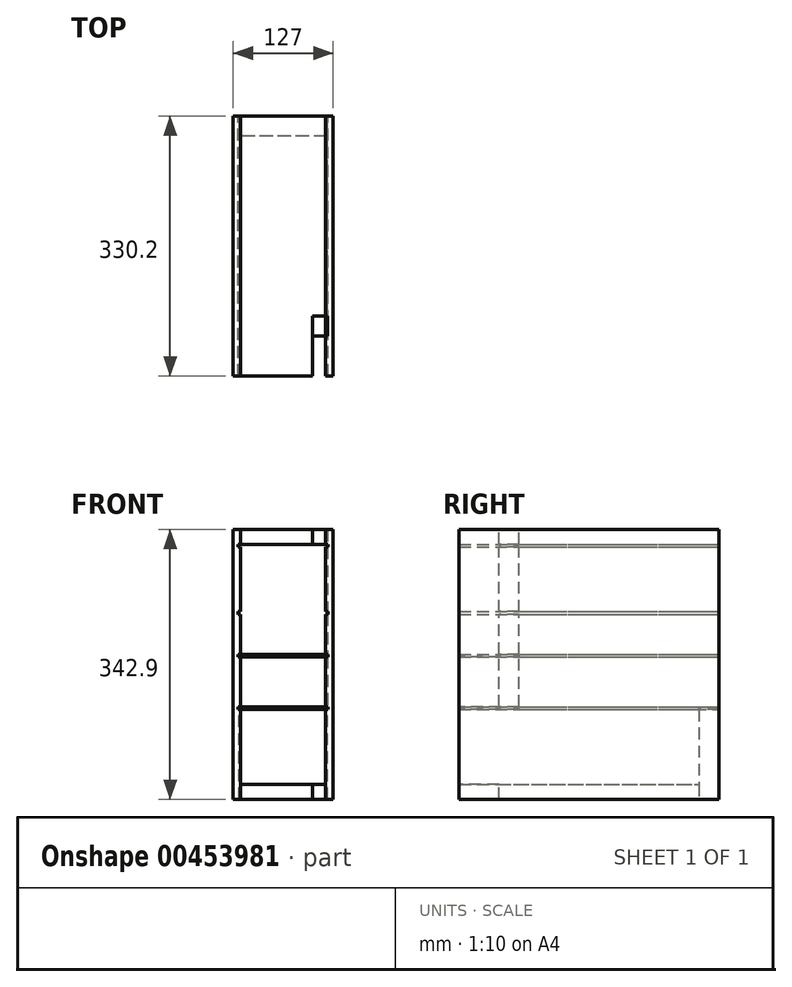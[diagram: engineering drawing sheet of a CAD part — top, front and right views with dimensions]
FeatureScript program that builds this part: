
annotation { "Feature Type Name" : "Feature", "Feature Type Description" : "" }
export const myFeature = defineFeature(function(context is Context, id is Id, definition is map)
    precondition{}
    {
        {
            var Q0;
            Q0=qCreatedBy(makeId("Front.planeOp"),FACE);
            var sketch = newSketch(context, id + "F0", { "sketchPlane" : qUnion([Q0])});
            skLineSegment(sketch, "E0.bottom", {"start": v(0, 0) * mm, "end": v(9.52, 0) * mm});
            skLineSegment(sketch, "E0.top", {"start": v(0, 342.9) * mm, "end": v(9.52, 342.9) * mm});
            skLineSegment(sketch, "E0.left", {"start": v(0, 0) * mm, "end": v(0, 342.9) * mm});
            skLineSegment(sketch, "E0.right", {"start": v(9.52, 0) * mm, "end": v(9.52, 342.9) * mm});
            skLineSegment(sketch, "E1.bottom", {"start": v(9.52, 0) * mm, "end": v(117.48, 0) * mm});
            skLineSegment(sketch, "E1.top", {"start": v(9.52, 19.05) * mm, "end": v(117.48, 19.05) * mm});
            skLineSegment(sketch, "E1.left", {"start": v(9.52, 0) * mm, "end": v(9.52, 19.05) * mm});
            skLineSegment(sketch, "E1.right", {"start": v(117.48, 0) * mm, "end": v(117.48, 19.05) * mm});
            skLineSegment(sketch, "E2.bottom", {"start": v(117.48, 0) * mm, "end": v(127, 0) * mm});
            skLineSegment(sketch, "E2.top", {"start": v(117.47, 342.9) * mm, "end": v(127, 342.9) * mm});
            skLineSegment(sketch, "E2.left", {"start": v(117.48, 0) * mm, "end": v(117.47, 342.9) * mm});
            skLineSegment(sketch, "E2.right", {"start": v(127, 0) * mm, "end": v(127, 342.9) * mm});
            skLineSegment(sketch, "E3.bottom", {"start": v(9.52, 342.9) * mm, "end": v(117.47, 342.9) * mm});
            skLineSegment(sketch, "E3.top", {"start": v(9.52, 323.85) * mm, "end": v(117.47, 323.85) * mm});
            skLineSegment(sketch, "E3.left", {"start": v(9.52, 342.9) * mm, "end": v(9.52, 323.85) * mm});
            skLineSegment(sketch, "E3.right", {"start": v(117.47, 342.9) * mm, "end": v(117.47, 323.85) * mm});
            skLineSegment(sketch, "E4.bottom", {"start": v(117.47, 117.6) * mm, "end": v(120.65, 117.6) * mm});
            skLineSegment(sketch, "E4.top", {"start": v(117.47, 114.3) * mm, "end": v(120.65, 114.3) * mm});
            skLineSegment(sketch, "E4.left", {"start": v(117.47, 117.6) * mm, "end": v(117.47, 114.3) * mm});
            skLineSegment(sketch, "E4.right", {"start": v(120.65, 117.6) * mm, "end": v(120.65, 114.3) * mm});
            skLineSegment(sketch, "E5.bottom", {"start": v(9.52, 114.3) * mm, "end": v(6.35, 114.3) * mm});
            skLineSegment(sketch, "E5.top", {"start": v(9.52, 117.6) * mm, "end": v(6.35, 117.6) * mm});
            skLineSegment(sketch, "E5.left", {"start": v(9.52, 114.3) * mm, "end": v(9.52, 117.6) * mm});
            skLineSegment(sketch, "E5.right", {"start": v(6.35, 114.3) * mm, "end": v(6.35, 117.6) * mm});
            skLineSegment(sketch, "E6", {"start": v(9.52, 114.3) * mm, "end": v(117.47, 114.3) * mm, "construction": true});
            skLineSegment(sketch, "E7", {"start": v(117.47, 117.6) * mm, "end": v(9.52, 117.6) * mm, "construction": true});
            skLineSegment(sketch, "E8.bottom", {"start": v(9.52, 184.4) * mm, "end": v(6.35, 184.4) * mm});
            skLineSegment(sketch, "E8.top", {"start": v(9.52, 181.1) * mm, "end": v(6.35, 181.1) * mm});
            skLineSegment(sketch, "E8.left", {"start": v(9.52, 184.4) * mm, "end": v(9.52, 181.1) * mm});
            skLineSegment(sketch, "E8.right", {"start": v(6.35, 184.4) * mm, "end": v(6.35, 181.1) * mm});
            skLineSegment(sketch, "E9.bottom", {"start": v(117.47, 184.4) * mm, "end": v(120.65, 184.4) * mm});
            skLineSegment(sketch, "E9.top", {"start": v(117.47, 181.1) * mm, "end": v(120.65, 181.1) * mm});
            skLineSegment(sketch, "E9.left", {"start": v(117.47, 184.4) * mm, "end": v(117.47, 181.1) * mm});
            skLineSegment(sketch, "E9.right", {"start": v(120.65, 184.4) * mm, "end": v(120.65, 181.1) * mm});
            skLineSegment(sketch, "E10", {"start": v(9.52, 181.1) * mm, "end": v(117.47, 181.1) * mm, "construction": true});
            skLineSegment(sketch, "E11", {"start": v(117.47, 184.4) * mm, "end": v(9.52, 184.4) * mm, "construction": true});
            skLineSegment(sketch, "E12", {"start": v(6.35, 117.6) * mm, "end": v(6.35, 181.1) * mm, "construction": true});
            skLineSegment(sketch, "E13", {"start": v(120.65, 117.6) * mm, "end": v(120.65, 181.1) * mm, "construction": true});
            skLineSegment(sketch, "E14", {"start": v(6.35, 184.4) * mm, "end": v(6.35, 235.2) * mm, "construction": true});
            skLineSegment(sketch, "E15", {"start": v(120.65, 184.4) * mm, "end": v(120.65, 235.2) * mm, "construction": true});
            skLineSegment(sketch, "E16.bottom", {"start": v(6.35, 235.2) * mm, "end": v(120.65, 235.2) * mm});
            skLineSegment(sketch, "E16.top", {"start": v(6.35, 238.5) * mm, "end": v(120.65, 238.5) * mm});
            skLineSegment(sketch, "E16.left", {"start": v(6.35, 235.2) * mm, "end": v(6.35, 238.5) * mm});
            skLineSegment(sketch, "E16.right", {"start": v(120.65, 235.2) * mm, "end": v(120.65, 238.5) * mm});
            skLineSegment(sketch, "E17", {"start": v(6.35, 238.5) * mm, "end": v(6.35, 320.55) * mm, "construction": true});
            skLineSegment(sketch, "E18", {"start": v(120.65, 238.5) * mm, "end": v(120.65, 320.55) * mm, "construction": true});
            skLineSegment(sketch, "E19.bottom", {"start": v(6.35, 320.55) * mm, "end": v(120.65, 320.55) * mm});
            skLineSegment(sketch, "E19.top", {"start": v(6.35, 323.85) * mm, "end": v(120.65, 323.85) * mm});
            skLineSegment(sketch, "E19.left", {"start": v(6.35, 320.55) * mm, "end": v(6.35, 323.85) * mm});
            skLineSegment(sketch, "E19.right", {"start": v(120.65, 320.55) * mm, "end": v(120.65, 323.85) * mm});
            skSolve(sketch);
        }
        {
            var Q0;
            Q0=makeQuery(id+"F0.imprint","IMPRINT",FACE,{"disambiguationData":[TD([[makeQuery(id+"F0.imprint","IMPRINT",EDGE,{"derivedFrom":sQuery(id+"F0.wireOp",EDGE,"E0.bottom")}),1.0]])]});
            var Q1;
            {var subQ3=sQuery(id+"F0.wireOp",EDGE,"E2.bottom");Q1=makeQuery(id+"F0.imprint","IMPRINT",FACE,{"disambiguationData":[TD([[makeQuery(id+"F0.imprint","IMPRINT",EDGE,{"derivedFrom":subQ3}),1.0]])]});}
            extrude(context, id + "F1", {"entities" : qUnion([Q0, Q1]), "depth" : 330.2 * mm});
        }
        {
            var Q0;
            {var subQ0=sQuery(id+"F0.wireOp",EDGE,"E1.bottom");Q0=makeQuery(id+"F0.imprint","IMPRINT",FACE,{"disambiguationData":[TD([[makeQuery(id+"F0.imprint","IMPRINT",EDGE,{"derivedFrom":subQ0}),1.0]])]});}
            var Q1;
            Q1=makeQuery(id+"F0.imprint","IMPRINT",FACE,{"disambiguationData":[TD([[makeQuery(id+"F0.imprint","IMPRINT",EDGE,{"derivedFrom":sQuery(id+"F0.wireOp",EDGE,"E3.bottom")}),-1.0]])]});
            var Q2;
            Q2=makeQuery(id+"F1.opExtrude","CAP_FACE",FACE,{"disambiguationData":[OSD([sQuery(id+"F0.wireOp",EDGE,"E2.bottom"),sQuery(id+"F0.wireOp",EDGE,"E2.top"),sQuery(id+"F0.wireOp",EDGE,"E2.left"),sQuery(id+"F0.wireOp",EDGE,"E2.right"),sQuery(id+"F0.wireOp",EDGE,"E3.right")])],"isStart":false});
            extrude(context, id + "F2", {"entities" : qUnion([Q0, Q1]), "endBound" : BoundingType.UP_TO_SURFACE, "endBoundEntityFace" : qUnion([Q2]), "depth" : 25.4 * mm});
        }
        {
            var Q0;
            Q0=qCreatedBy(makeId("Front.planeOp"),FACE);
            var sketch = newSketch(context, id + "F3", { "sketchPlane" : qUnion([Q0])});
            skLineSegment(sketch, "E20.bottom", {"start": v(7.37, 114.3) * mm, "end": v(119.63, 114.3) * mm});
            skLineSegment(sketch, "E20.top", {"start": v(7.37, 117.48) * mm, "end": v(119.63, 117.48) * mm});
            skLineSegment(sketch, "E20.left", {"start": v(7.37, 114.3) * mm, "end": v(7.37, 117.48) * mm});
            skLineSegment(sketch, "E20.right", {"start": v(119.63, 114.3) * mm, "end": v(119.63, 117.48) * mm});
            skLineSegment(sketch, "E21", {"start": v(7.37, 117.48) * mm, "end": v(7.37, 181.1) * mm, "construction": true});
            skLineSegment(sketch, "E22", {"start": v(119.63, 117.48) * mm, "end": v(119.63, 181.1) * mm, "construction": true});
            skLineSegment(sketch, "E23.bottom", {"start": v(7.37, 181.1) * mm, "end": v(119.63, 181.1) * mm});
            skLineSegment(sketch, "E23.top", {"start": v(7.37, 184.28) * mm, "end": v(119.63, 184.28) * mm});
            skLineSegment(sketch, "E23.left", {"start": v(7.37, 181.1) * mm, "end": v(7.37, 184.28) * mm});
            skLineSegment(sketch, "E23.right", {"start": v(119.63, 181.1) * mm, "end": v(119.63, 184.28) * mm});
            skSolve(sketch);
        }
        {
            var Q0;
            Q0 = qSketchRegion(id + "F3", true);
            var Q1;
            Q1=makeQuery(id+"F1.opExtrude","CAP_FACE",FACE,{"disambiguationData":[OSD([sQuery(id+"F0.wireOp",EDGE,"E2.bottom"),sQuery(id+"F0.wireOp",EDGE,"E2.top"),sQuery(id+"F0.wireOp",EDGE,"E2.left"),sQuery(id+"F0.wireOp",EDGE,"E2.right"),sQuery(id+"F0.wireOp",EDGE,"E3.right"),sQuery(id+"F0.wireOp",EDGE,"E4.bottom"),sQuery(id+"F0.wireOp",EDGE,"E4.top"),sQuery(id+"F0.wireOp",EDGE,"E4.right")])],"isStart":false});
            extrude(context, id + "F4", {"entities" : qUnion([Q0]), "endBound" : BoundingType.UP_TO_SURFACE, "endBoundEntityFace" : qUnion([Q1]), "depth" : 25.4 * mm});
        }
        {
            var Q0;
            Q0=makeQuery(id+"F4.opExtrude","SWEPT_FACE",FACE,{"disambiguationData":[OSD([sQuery(id+"F3.wireOp",EDGE,"E20.top")])]});
            var sketch = newSketch(context, id + "F5", { "sketchPlane" : qUnion([Q0])});
            skLineSegment(sketch, "E24.bottom", {"start": v(119.63, -254) * mm, "end": v(100.58, -254) * mm});
            skLineSegment(sketch, "E24.top", {"start": v(119.63, -279.4) * mm, "end": v(100.58, -279.4) * mm});
            skLineSegment(sketch, "E24.left", {"start": v(119.63, -254) * mm, "end": v(119.63, -279.4) * mm});
            skLineSegment(sketch, "E24.right", {"start": v(100.58, -254) * mm, "end": v(100.58, -279.4) * mm});
            skSolve(sketch);
        }
        {
            var Q0;
            Q0 = qSketchRegion(id + "F5", true);
            extrude(context, id + "F6", {"entities" : qUnion([Q0]), "operationType" : NewBodyOperationType.REMOVE, "endBound" : BoundingType.UP_TO_NEXT, "oppositeDirection" : true, "depth" : 25.4 * mm});
        }
        {
            var Q0;
            Q0=makeQuery(id+"F5.imprint","IMPRINT",FACE,{"disambiguationData":[TD([[makeQuery(id+"F5.imprint","IMPRINT",EDGE,{"derivedFrom":sQuery(id+"F5.wireOp",EDGE,"E24.bottom")}),1.0]])]});
            extrude(context, id + "F7", {"entities" : qUnion([Q0]), "operationType" : NewBodyOperationType.REMOVE, "endBound" : BoundingType.THROUGH_ALL, "depth" : 25.4 * mm});
        }
        {
            var Q0;
            Q0=makeQuery(id+"F2.opExtrude","SWEPT_FACE",FACE,{"disambiguationData":[OSD([sQuery(id+"F0.wireOp",EDGE,"E3.bottom")])]});
            var sketch = newSketch(context, id + "F8", { "sketchPlane" : qUnion([Q0])});
            skLineSegment(sketch, "E25.bottom", {"start": v(100.58, -279.4) * mm, "end": v(117.47, -279.4) * mm});
            skLineSegment(sketch, "E25.top", {"start": v(100.58, -330.2) * mm, "end": v(117.47, -330.2) * mm});
            skLineSegment(sketch, "E25.left", {"start": v(100.58, -279.4) * mm, "end": v(100.58, -330.2) * mm});
            skLineSegment(sketch, "E25.right", {"start": v(117.47, -279.4) * mm, "end": v(117.47, -330.2) * mm});
            skSolve(sketch);
        }
        {
            var Q0;
            Q0 = qSketchRegion(id + "F8", true);
            extrude(context, id + "F9", {"entities" : qUnion([Q0]), "operationType" : NewBodyOperationType.REMOVE, "endBound" : BoundingType.THROUGH_ALL, "oppositeDirection" : true, "depth" : 25.4 * mm});
        }
        {
            var Q0;
            {var subQ3=sQuery(id+"F5.wireOp",EDGE,"E24.bottom");Q0=makeQuery(id+"F5.imprint","IMPRINT",FACE,{"disambiguationData":[TD([[makeQuery(id+"F5.imprint","IMPRINT",EDGE,{"derivedFrom":subQ3}),-1.0]])]});}
            var sketch = newSketch(context, id + "F10", { "sketchPlane" : qUnion([Q0])});
            skLineSegment(sketch, "E26.bottom", {"start": v(119.63, 0) * mm, "end": v(7.37, 0) * mm});
            skLineSegment(sketch, "E26.top", {"start": v(119.63, -25.4) * mm, "end": v(7.37, -25.4) * mm});
            skLineSegment(sketch, "E26.left", {"start": v(119.63, 0) * mm, "end": v(119.63, -25.4) * mm});
            skLineSegment(sketch, "E26.right", {"start": v(7.37, 0) * mm, "end": v(7.37, -25.4) * mm});
            skSolve(sketch);
        }
        {
            var Q0;
            Q0 = qSketchRegion(id + "F10", true);
            extrude(context, id + "F11", {"entities" : qUnion([Q0]), "operationType" : NewBodyOperationType.REMOVE, "endBound" : BoundingType.THROUGH_ALL, "oppositeDirection" : true, "depth" : 25.4 * mm});
        }
    });
